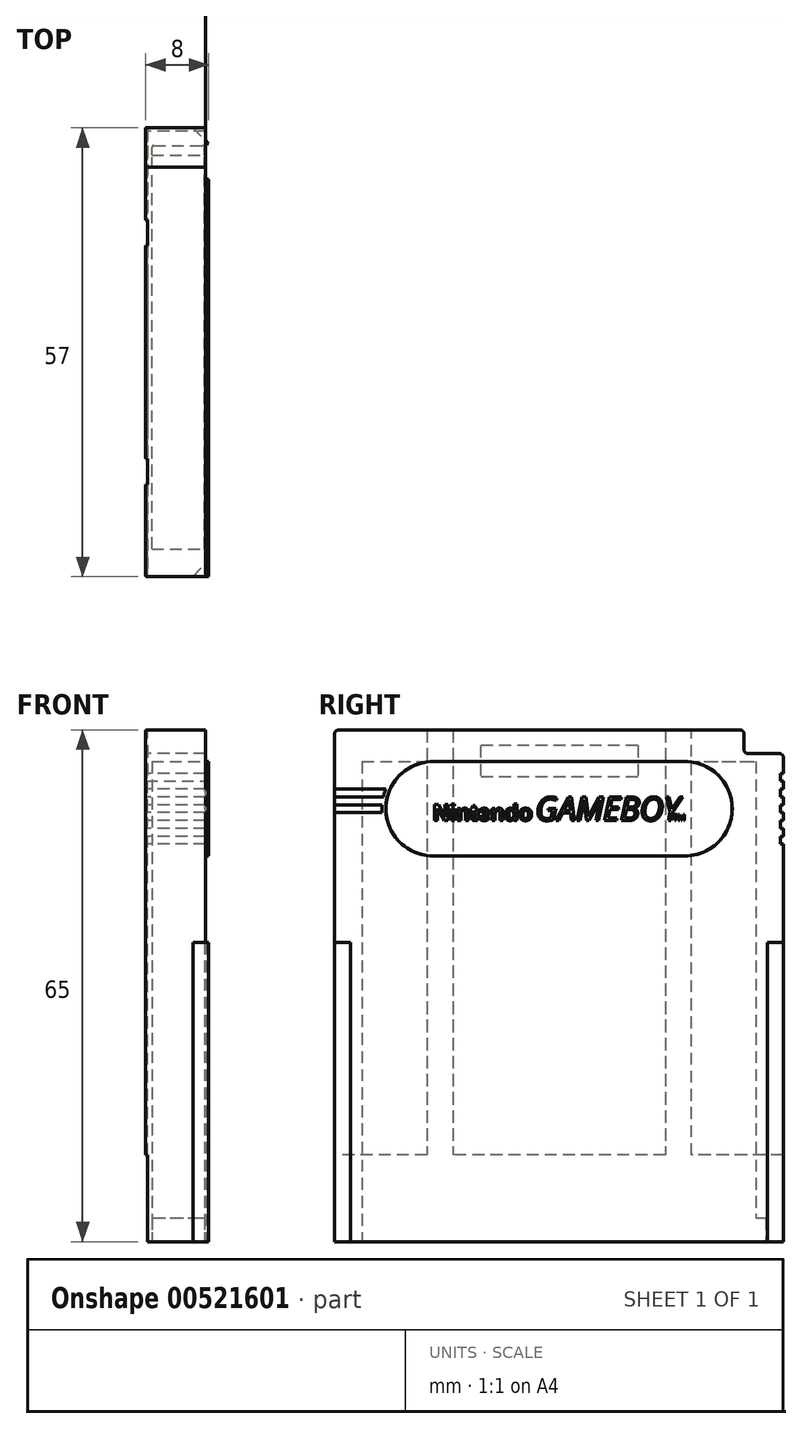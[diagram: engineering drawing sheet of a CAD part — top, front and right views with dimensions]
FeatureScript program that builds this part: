
annotation { "Feature Type Name" : "Feature", "Feature Type Description" : "" }
export const myFeature = defineFeature(function(context is Context, id is Id, definition is map)
    precondition{}
    {
        {
            var Q0;
            Q0=qCreatedBy(makeId("Right.planeOp"),FACE);
            var sketch = newSketch(context, id + "F0", { "sketchPlane" : qUnion([Q0])});
            skLineSegment(sketch, "E0.bottom", {"start": v(-28.5, 32.5) * mm, "end": v(23.5, 32.5) * mm});
            skLineSegment(sketch, "E0.top", {"start": v(-28.5, -32.5) * mm, "end": v(28.5, -32.5) * mm});
            skLineSegment(sketch, "E0.left", {"start": v(-28.5, 32.5) * mm, "end": v(-28.5, -32.5) * mm});
            skLineSegment(sketch, "E0.right", {"start": v(28.5, 29.5) * mm, "end": v(28.5, -32.5) * mm});
            skPoint(sketch, "E0.middle", {"position": v(0, 0) * mm});
            skLineSegment(sketch, "E1", {"start": v(23.5, 32.5) * mm, "end": v(23.5, 29.5) * mm});
            skLineSegment(sketch, "E2", {"start": v(23.5, 29.5) * mm, "end": v(28.5, 29.5) * mm});
            skSolve(sketch);
        }
        {
            var Q0;
            Q0=makeQuery(id+"F0.imprint","IMPRINT",FACE,{"disambiguationData":[TD([[makeQuery(id+"F0.imprint","IMPRINT",EDGE,{"derivedFrom":sQuery(id+"F0.wireOp",EDGE,"E0.bottom")}),-1.0]])]});
            extrude(context, id + "F1", {"entities" : qUnion([Q0]), "endBound" : BoundingType.SYMMETRIC, "depth" : 7.75 * mm, "offsetDistance" : 25 * mm});
        }
        {
            var Q0;
            Q0=makeQuery(id+"F1.opExtrude","SWEPT_FACE",FACE,{"disambiguationData":[OSD([sQuery(id+"F0.wireOp",EDGE,"E0.top")])]});
            var sketch = newSketch(context, id + "F2", { "sketchPlane" : qUnion([Q0])});
            skLineSegment(sketch, "E3", {"start": v(1.88, 28.5) * mm, "end": v(3.88, 26.5) * mm});
            skLineSegment(sketch, "E4", {"start": v(3.88, 26.5) * mm, "end": v(3.88, 28.5) * mm});
            skLineSegment(sketch, "E5", {"start": v(3.88, 28.5) * mm, "end": v(1.88, 28.5) * mm});
            skLineSegment(sketch, "E6", {"start": v(1.88, -28.5) * mm, "end": v(3.88, -26.5) * mm});
            skLineSegment(sketch, "E7", {"start": v(3.88, -26.5) * mm, "end": v(3.88, -28.5) * mm});
            skLineSegment(sketch, "E8", {"start": v(3.88, -28.5) * mm, "end": v(1.88, -28.5) * mm});
            skSolve(sketch);
        }
        {
            var Q0;
            Q0 = qSketchRegion(id + "F2", true);
            extrude(context, id + "F3", {"entities" : qUnion([Q0]), "operationType" : NewBodyOperationType.REMOVE, "oppositeDirection" : true, "depth" : 38 * mm, "offsetDistance" : 25 * mm});
        }
        {
            var Q0;
            Q0=makeQuery(id+"F1.opExtrude","CAP_FACE",FACE,{"disambiguationData":[OSD([sQuery(id+"F0.wireOp",EDGE,"E0.bottom"),sQuery(id+"F0.wireOp",EDGE,"E0.top"),sQuery(id+"F0.wireOp",EDGE,"E0.left"),sQuery(id+"F0.wireOp",EDGE,"E0.right"),sQuery(id+"F0.wireOp",EDGE,"E1"),sQuery(id+"F0.wireOp",EDGE,"E2")])],"isStart":true});
            var sketch = newSketch(context, id + "F4", { "sketchPlane" : qUnion([Q0])});
            skLineSegment(sketch, "E9.bottom", {"start": v(-13.5, 32.5) * mm, "end": v(13.5, 32.5) * mm});
            skLineSegment(sketch, "E9.top", {"start": v(-13.5, -21.5) * mm, "end": v(13.5, -21.5) * mm});
            skLineSegment(sketch, "E9.left", {"start": v(-13.5, 32.5) * mm, "end": v(-13.5, -21.5) * mm});
            skLineSegment(sketch, "E9.right", {"start": v(13.5, 32.5) * mm, "end": v(13.5, -21.5) * mm});
            skLineSegment(sketch, "E10.bottom", {"start": v(16.8, 32.5) * mm, "end": v(28.5, 32.5) * mm});
            skLineSegment(sketch, "E10.top", {"start": v(16.8, -21.5) * mm, "end": v(28.5, -21.5) * mm});
            skLineSegment(sketch, "E10.left", {"start": v(16.8, 32.5) * mm, "end": v(16.8, -21.5) * mm});
            skLineSegment(sketch, "E10.right", {"start": v(28.5, 32.5) * mm, "end": v(28.5, -21.5) * mm});
            skLineSegment(sketch, "E11.bottom", {"start": v(-28.5, -21.5) * mm, "end": v(-16.8, -21.5) * mm});
            skLineSegment(sketch, "E11.top", {"start": v(-23.5, 32.5) * mm, "end": v(-16.8, 32.5) * mm});
            skLineSegment(sketch, "E11.left", {"start": v(-28.5, -21.5) * mm, "end": v(-28.5, 29.5) * mm});
            skLineSegment(sketch, "E11.right", {"start": v(-16.8, -21.5) * mm, "end": v(-16.8, 32.5) * mm});
            skLineSegment(sketch, "E12", {"start": v(-28.5, 29.5) * mm, "end": v(-23.5, 29.5) * mm});
            skLineSegment(sketch, "E13", {"start": v(-23.5, 29.5) * mm, "end": v(-23.5, 32.5) * mm});
            skLineSegment(sketch, "E14.bottom", {"start": v(-10, 30.5) * mm, "end": v(10, 30.5) * mm});
            skLineSegment(sketch, "E14.top", {"start": v(-10, 26.5) * mm, "end": v(10, 26.5) * mm});
            skLineSegment(sketch, "E14.left", {"start": v(-10, 30.5) * mm, "end": v(-10, 26.5) * mm});
            skLineSegment(sketch, "E14.right", {"start": v(10, 30.5) * mm, "end": v(10, 26.5) * mm});
            skSolve(sketch);
        }
        {
            var Q0;
            Q0 = qSketchRegion(id + "F4", true);
            extrude(context, id + "F5", {"entities" : qUnion([Q0]), "operationType" : NewBodyOperationType.ADD, "depth" : .25 * mm, "offsetDistance" : 25 * mm});
        }
        {
            var Q0;
            Q0=makeQuery(id+"F1.opExtrude","CAP_FACE",FACE,{"disambiguationData":[OSD([sQuery(id+"F0.wireOp",EDGE,"E0.bottom"),sQuery(id+"F0.wireOp",EDGE,"E0.top"),sQuery(id+"F0.wireOp",EDGE,"E0.left"),sQuery(id+"F0.wireOp",EDGE,"E0.right"),sQuery(id+"F0.wireOp",EDGE,"E1"),sQuery(id+"F0.wireOp",EDGE,"E2")])],"isStart":false});
            var sketch = newSketch(context, id + "F6", { "sketchPlane" : qUnion([Q0])});
            skLineSegment(sketch, "E15.bottom", {"start": v(-16, 28.5) * mm, "end": v(16, 28.5) * mm});
            skLineSegment(sketch, "E15.top", {"start": v(-16, 16.5) * mm, "end": v(16, 16.5) * mm});
            skPoint(sketch, "E15.middle", {"position": v(0, 22.5) * mm});
            skArc(sketch, "E16", {"start": v(16, 16.5) * mm, "mid": v(22, 22.5) * mm, "end": v(16, 28.5) * mm});
            skArc(sketch, "E17", {"start": v(-16, 28.5) * mm, "mid": v(-22, 22.5) * mm, "end": v(-16, 16.5) * mm});
            skSolve(sketch);
        }
        {
            var Q0;
            Q0=makeQuery(id+"F6.imprint","IMPRINT",FACE,{"disambiguationData":[TD([[makeQuery(id+"F6.imprint","IMPRINT",EDGE,{"derivedFrom":sQuery(id+"F6.wireOp",EDGE,"E15.bottom")}),-1.0]])]});
            extrude(context, id + "F7", {"entities" : qUnion([Q0]), "operationType" : NewBodyOperationType.REMOVE, "oppositeDirection" : true, "depth" : .4 * mm, "offsetDistance" : 25 * mm});
        }
        {
            var Q0;
            Q0=makeQuery(id+"F7.boolean.opBoolean","COPY",FACE,{"derivedFrom":makeQuery(id+"F7.opExtrude","CAP_FACE",FACE,{"disambiguationData":[OSD([sQuery(id+"F6.wireOp",EDGE,"E15.bottom"),sQuery(id+"F6.wireOp",EDGE,"E15.top"),sQuery(id+"F6.wireOp",EDGE,"E16"),sQuery(id+"F6.wireOp",EDGE,"E17")])],"isStart":false})});
            fillet(context, id + "F8", {"entities" : qUnion([Q0]), "radius" : 10 * mm, "rho" : .5, "crossSection" : FilletCrossSection.CONIC, "allowEdgeOverflow" : false});
        }
        {
            var Q0;
            Q0=makeQuery(id+"F1.opExtrude","CAP_FACE",FACE,{"disambiguationData":[OSD([sQuery(id+"F0.wireOp",EDGE,"E0.bottom"),sQuery(id+"F0.wireOp",EDGE,"E0.top"),sQuery(id+"F0.wireOp",EDGE,"E0.left"),sQuery(id+"F0.wireOp",EDGE,"E0.right"),sQuery(id+"F0.wireOp",EDGE,"E1"),sQuery(id+"F0.wireOp",EDGE,"E2")])],"isStart":false});
            var sketch = newSketch(context, id + "F9", { "sketchPlane" : qUnion([Q0])});
            skArc(sketch, "E18", {"start": v(20.7, 18) * mm, "mid": v(21.1, 18.48) * mm, "end": v(21.48, 19) * mm});
            skLineSegment(sketch, "E19", {"start": v(20.7, 27) * mm, "end": v(28.5, 27) * mm});
            skLineSegment(sketch, "E20", {"start": v(28.5, 27) * mm, "end": v(28.5, 26) * mm});
            skLineSegment(sketch, "E21", {"start": v(28.5, 26) * mm, "end": v(21.48, 26) * mm});
            skLineSegment(sketch, "E22", {"start": v(22, 25) * mm, "end": v(28.5, 25) * mm});
            skLineSegment(sketch, "E23", {"start": v(28.5, 25) * mm, "end": v(28.5, 24) * mm});
            skLineSegment(sketch, "E24", {"start": v(28.5, 24) * mm, "end": v(22.32, 24) * mm});
            skLineSegment(sketch, "E25", {"start": v(22.48, 23) * mm, "end": v(28.5, 23) * mm});
            skLineSegment(sketch, "E26", {"start": v(28.5, 23) * mm, "end": v(28.5, 22) * mm});
            skLineSegment(sketch, "E27", {"start": v(28.5, 22) * mm, "end": v(22.48, 22) * mm});
            skLineSegment(sketch, "E28", {"start": v(22.32, 21) * mm, "end": v(28.5, 21) * mm});
            skLineSegment(sketch, "E29", {"start": v(21.48, 19) * mm, "end": v(28.5, 19) * mm});
            skLineSegment(sketch, "E30", {"start": v(28.5, 21) * mm, "end": v(28.5, 20) * mm});
            skLineSegment(sketch, "E31", {"start": v(28.5, 20) * mm, "end": v(22, 20) * mm});
            skLineSegment(sketch, "E32", {"start": v(28.5, 19) * mm, "end": v(28.5, 18) * mm});
            skLineSegment(sketch, "E33", {"start": v(28.5, 18) * mm, "end": v(20.7, 18) * mm});
            skArc(sketch, "E34.trimOffspring", {"start": v(21.48, 26) * mm, "mid": v(21.1, 26.52) * mm, "end": v(20.7, 27) * mm});
            skArc(sketch, "E35.trimOffspring", {"start": v(22.32, 24) * mm, "mid": v(22.18, 24.5) * mm, "end": v(22, 25) * mm});
            skArc(sketch, "E36.trimOffspring", {"start": v(22.48, 22) * mm, "mid": v(22.5, 22.5) * mm, "end": v(22.48, 23) * mm});
            skArc(sketch, "E37.trimOffspring", {"start": v(22, 20) * mm, "mid": v(22.18, 20.5) * mm, "end": v(22.32, 21) * mm});
            skArc(sketch, "E38.MirrorCS", {"start": v(-22.48, 22) * mm, "mid": v(-22.5, 22.5) * mm, "end": v(-22.48, 23) * mm});
            skLineSegment(sketch, "E39.MirrorCS", {"start": v(-28.5, 23) * mm, "end": v(-28.5, 22) * mm});
            skLineSegment(sketch, "E40.MirrorCS", {"start": v(-28.5, 21) * mm, "end": v(-28.5, 20) * mm});
            skArc(sketch, "E41.MirrorCS", {"start": v(-22, 20) * mm, "mid": v(-22.18, 20.5) * mm, "end": v(-22.32, 21) * mm});
            skArc(sketch, "E42.MirrorCS", {"start": v(-22.32, 24) * mm, "mid": v(-22.18, 24.5) * mm, "end": v(-22, 25) * mm});
            skLineSegment(sketch, "E43.MirrorCS", {"start": v(-28.5, 19) * mm, "end": v(-28.5, 18) * mm});
            skLineSegment(sketch, "E44.MirrorCS", {"start": v(-28.5, 25) * mm, "end": v(-28.5, 24) * mm});
            skLineSegment(sketch, "E45.MirrorCS", {"start": v(-28.5, 27) * mm, "end": v(-28.5, 26) * mm});
            skArc(sketch, "E46.MirrorCS", {"start": v(-21.48, 26) * mm, "mid": v(-21.1, 26.52) * mm, "end": v(-20.7, 27) * mm});
            skArc(sketch, "E47.MirrorCS", {"start": v(-20.7, 18) * mm, "mid": v(-21.1, 18.48) * mm, "end": v(-21.48, 19) * mm});
            skLineSegment(sketch, "E48.MirrorCS", {"start": v(-28.5, 18) * mm, "end": v(-20.7, 18) * mm});
            skLineSegment(sketch, "E49.MirrorCS", {"start": v(-20.7, 27) * mm, "end": v(-28.5, 27) * mm});
            skLineSegment(sketch, "E50.MirrorCS", {"start": v(-28.5, 26) * mm, "end": v(-21.48, 26) * mm});
            skLineSegment(sketch, "E51.MirrorCS", {"start": v(-22, 25) * mm, "end": v(-28.5, 25) * mm});
            skLineSegment(sketch, "E52.MirrorCS", {"start": v(-28.5, 24) * mm, "end": v(-22.32, 24) * mm});
            skLineSegment(sketch, "E53.MirrorCS", {"start": v(-22.48, 23) * mm, "end": v(-28.5, 23) * mm});
            skLineSegment(sketch, "E54.MirrorCS", {"start": v(-21.48, 19) * mm, "end": v(-28.5, 19) * mm});
            skLineSegment(sketch, "E55.MirrorCS", {"start": v(-28.5, 20) * mm, "end": v(-22, 20) * mm});
            skLineSegment(sketch, "E56.MirrorCS", {"start": v(-22.32, 21) * mm, "end": v(-28.5, 21) * mm});
            skLineSegment(sketch, "E57.MirrorCS", {"start": v(-28.5, 22) * mm, "end": v(-22.48, 22) * mm});
            skSolve(sketch);
        }
        {
            var Q0;
            Q0=makeQuery(id+"F9.imprint","IMPRINT",FACE,{"disambiguationData":[TD([[makeQuery(id+"F9.imprint","IMPRINT",EDGE,{"derivedFrom":sQuery(id+"F9.wireOp",EDGE,"E43.MirrorCS")}),1.0]])]});
            var Q1;
            Q1=makeQuery(id+"F9.imprint","IMPRINT",FACE,{"disambiguationData":[TD([[makeQuery(id+"F9.imprint","IMPRINT",EDGE,{"derivedFrom":sQuery(id+"F9.wireOp",EDGE,"E40.MirrorCS")}),1.0]])]});
            var Q2;
            Q2=makeQuery(id+"F9.imprint","IMPRINT",FACE,{"disambiguationData":[TD([[makeQuery(id+"F9.imprint","IMPRINT",EDGE,{"derivedFrom":sQuery(id+"F9.wireOp",EDGE,"E38.MirrorCS")}),1.0]])]});
            var Q3;
            Q3=makeQuery(id+"F9.imprint","IMPRINT",FACE,{"disambiguationData":[TD([[makeQuery(id+"F9.imprint","IMPRINT",EDGE,{"derivedFrom":sQuery(id+"F9.wireOp",EDGE,"E42.MirrorCS")}),1.0]])]});
            var Q4;
            Q4=makeQuery(id+"F9.imprint","IMPRINT",FACE,{"disambiguationData":[TD([[makeQuery(id+"F9.imprint","IMPRINT",EDGE,{"derivedFrom":sQuery(id+"F9.wireOp",EDGE,"E45.MirrorCS")}),1.0]])]});
            var Q5;
            Q5=makeQuery(id+"F9.imprint","IMPRINT",FACE,{"disambiguationData":[TD([[makeQuery(id+"F9.imprint","IMPRINT",EDGE,{"derivedFrom":sQuery(id+"F9.wireOp",EDGE,"E19")}),-1.0]])]});
            var Q6;
            Q6=makeQuery(id+"F9.imprint","IMPRINT",FACE,{"disambiguationData":[TD([[makeQuery(id+"F9.imprint","IMPRINT",EDGE,{"derivedFrom":sQuery(id+"F9.wireOp",EDGE,"E22")}),-1.0]])]});
            var Q7;
            Q7=makeQuery(id+"F9.imprint","IMPRINT",FACE,{"disambiguationData":[TD([[makeQuery(id+"F9.imprint","IMPRINT",EDGE,{"derivedFrom":sQuery(id+"F9.wireOp",EDGE,"E25")}),-1.0]])]});
            var Q8;
            Q8=makeQuery(id+"F9.imprint","IMPRINT",FACE,{"disambiguationData":[TD([[makeQuery(id+"F9.imprint","IMPRINT",EDGE,{"derivedFrom":sQuery(id+"F9.wireOp",EDGE,"E28")}),-1.0]])]});
            var Q9;
            Q9=makeQuery(id+"F9.imprint","IMPRINT",FACE,{"disambiguationData":[TD([[makeQuery(id+"F9.imprint","IMPRINT",EDGE,{"derivedFrom":sQuery(id+"F9.wireOp",EDGE,"E18")}),-1.0]])]});
            extrude(context, id + "F10", {"entities" : qUnion([Q0, Q1, Q2, Q3, Q4, Q5, Q6, Q7, Q8, Q9]), "operationType" : NewBodyOperationType.REMOVE, "oppositeDirection" : true, "depth" : .4 * mm, "offsetDistance" : 25 * mm});
        }
        {
            var Q0;
            Q0=makeQuery(id+"F5.boolean.opBoolean","MERGE",FACE,{"derivedFrom":[makeQuery(id+"F1.opExtrude","SWEPT_FACE",FACE,{"disambiguationData":[OSD([sQuery(id+"F0.wireOp",EDGE,"E0.right")])]}),makeQuery(id+"F5.opExtrude","SWEPT_FACE",FACE,{"disambiguationData":[OSD([sQuery(id+"F4.wireOp",EDGE,"E11.left")])]})]});
            var sketch = newSketch(context, id + "F11", { "sketchPlane" : qUnion([Q0])});
            skLineSegment(sketch, "E58", {"start": v(-3.48, 27) * mm, "end": v(4.12, 27) * mm});
            skLineSegment(sketch, "E59", {"start": v(4.12, 27) * mm, "end": v(4.12, 26) * mm});
            skLineSegment(sketch, "E60", {"start": v(4.12, 26) * mm, "end": v(-3.47, 26) * mm});
            skLineSegment(sketch, "E61", {"start": v(-3.47, 26) * mm, "end": v(-3.47, 27) * mm});
            skLineSegment(sketch, "E62.bottom", {"start": v(-3.48, 25) * mm, "end": v(4.12, 25) * mm});
            skLineSegment(sketch, "E62.top", {"start": v(-3.48, 24) * mm, "end": v(4.12, 24) * mm});
            skLineSegment(sketch, "E62.left", {"start": v(-3.47, 25) * mm, "end": v(-3.47, 24) * mm});
            skLineSegment(sketch, "E62.right", {"start": v(4.12, 25) * mm, "end": v(4.12, 24) * mm});
            skLineSegment(sketch, "E63.bottom", {"start": v(-3.48, 23) * mm, "end": v(4.12, 23) * mm});
            skLineSegment(sketch, "E63.top", {"start": v(-3.48, 22) * mm, "end": v(4.12, 22) * mm});
            skLineSegment(sketch, "E63.left", {"start": v(-3.48, 23) * mm, "end": v(-3.48, 22) * mm});
            skLineSegment(sketch, "E63.right", {"start": v(4.12, 23) * mm, "end": v(4.12, 22) * mm});
            skLineSegment(sketch, "E64.bottom", {"start": v(-3.48, 21) * mm, "end": v(4.12, 21) * mm});
            skLineSegment(sketch, "E64.top", {"start": v(-3.48, 20) * mm, "end": v(4.12, 20) * mm});
            skLineSegment(sketch, "E64.left", {"start": v(-3.47, 21) * mm, "end": v(-3.47, 20) * mm});
            skLineSegment(sketch, "E64.right", {"start": v(4.12, 21) * mm, "end": v(4.12, 20) * mm});
            skLineSegment(sketch, "E65.bottom", {"start": v(-3.48, 19) * mm, "end": v(4.12, 19) * mm});
            skLineSegment(sketch, "E65.top", {"start": v(-3.48, 18) * mm, "end": v(4.12, 18) * mm});
            skLineSegment(sketch, "E65.left", {"start": v(-3.47, 19) * mm, "end": v(-3.47, 18) * mm});
            skLineSegment(sketch, "E65.right", {"start": v(4.12, 19) * mm, "end": v(4.12, 18) * mm});
            skSolve(sketch);
        }
        {
            var Q0;
            Q0 = qSketchRegion(id + "F11", true);
            extrude(context, id + "F12", {"entities" : qUnion([Q0]), "operationType" : NewBodyOperationType.REMOVE, "oppositeDirection" : true, "depth" : .4 * mm, "offsetDistance" : 25 * mm});
        }
        {
            var Q0;
            Q0=makeQuery(id+"F5.boolean.opBoolean","MERGE",EDGE,{"derivedFrom":[makeQuery(id+"F1.opExtrude","SWEPT_EDGE",EDGE,{"disambiguationData":[OSD([sQuery(id+"F0.wireOp",EDGE,"E0.bottom"),sQuery(id+"F0.wireOp",EDGE,"E1")])]}),makeQuery(id+"F5.opExtrude","SWEPT_EDGE",EDGE,{"disambiguationData":[OSD([sQuery(id+"F4.wireOp",EDGE,"E11.top"),sQuery(id+"F4.wireOp",EDGE,"E13")])]})]});
            var Q1;
            Q1=makeQuery(id+"F5.boolean.opBoolean","MERGE",EDGE,{"derivedFrom":[makeQuery(id+"F1.opExtrude","SWEPT_EDGE",EDGE,{"disambiguationData":[OSD([sQuery(id+"F0.wireOp",EDGE,"E1"),sQuery(id+"F0.wireOp",EDGE,"E2")])]}),makeQuery(id+"F5.opExtrude","SWEPT_EDGE",EDGE,{"disambiguationData":[OSD([sQuery(id+"F4.wireOp",EDGE,"E12"),sQuery(id+"F4.wireOp",EDGE,"E13")])]})]});
            var Q2;
            Q2=makeQuery(id+"F5.boolean.opBoolean","MERGE",EDGE,{"derivedFrom":[makeQuery(id+"F1.opExtrude","SWEPT_EDGE",EDGE,{"disambiguationData":[OSD([sQuery(id+"F0.wireOp",EDGE,"E0.right"),sQuery(id+"F0.wireOp",EDGE,"E2")])]}),makeQuery(id+"F5.opExtrude","SWEPT_EDGE",EDGE,{"disambiguationData":[OSD([sQuery(id+"F4.wireOp",EDGE,"E11.left"),sQuery(id+"F4.wireOp",EDGE,"E12")])]})]});
            var Q3;
            Q3=makeQuery(id+"F5.boolean.opBoolean","MERGE",EDGE,{"derivedFrom":[makeQuery(id+"F1.opExtrude","SWEPT_EDGE",EDGE,{"disambiguationData":[OSD([sQuery(id+"F0.wireOp",EDGE,"E0.bottom"),sQuery(id+"F0.wireOp",EDGE,"E0.left")])]}),makeQuery(id+"F5.opExtrude","SWEPT_EDGE",EDGE,{"disambiguationData":[OSD([sQuery(id+"F4.wireOp",EDGE,"E10.bottom"),sQuery(id+"F4.wireOp",EDGE,"E10.right")])]})]});
            fillet(context, id + "F13", {"entities" : qUnion([Q0, Q1, Q2, Q3]), "radius" : .5 * mm, "tangentPropagation" : true, "allowEdgeOverflow" : false});
        }
        {
            var Q0;
            Q0=makeQuery(id+"F1.opExtrude","CAP_EDGE",EDGE,{"disambiguationData":[OSD([sQuery(id+"F0.wireOp",EDGE,"E0.bottom")])],"isStart":false});
            var Q1;
            Q1=makeQuery(id+"F1.opExtrude","CAP_EDGE",EDGE,{"disambiguationData":[OSD([sQuery(id+"F0.wireOp",EDGE,"E2")])],"isStart":false});
            var Q2;
            Q2=makeQuery(id+"F5.opExtrude","CAP_EDGE",EDGE,{"disambiguationData":[OSD([sQuery(id+"F4.wireOp",EDGE,"E12")])],"isStart":false});
            var Q3;
            Q3=makeQuery(id+"F5.opExtrude","CAP_EDGE",EDGE,{"disambiguationData":[OSD([sQuery(id+"F4.wireOp",EDGE,"E13")])],"isStart":false});
            var Q4;
            Q4=makeQuery(id+"F1.opExtrude","CAP_EDGE",EDGE,{"disambiguationData":[OSD([sQuery(id+"F0.wireOp",EDGE,"E1")])],"isStart":false});
            var Q5;
            Q5=makeQuery(id+"F5.opExtrude","CAP_EDGE",EDGE,{"disambiguationData":[OSD([sQuery(id+"F4.wireOp",EDGE,"E11.top")])],"isStart":false});
            var Q6;
            Q6=makeQuery(id+"F5.opExtrude","CAP_EDGE",EDGE,{"disambiguationData":[OSD([sQuery(id+"F4.wireOp",EDGE,"E9.bottom")])],"isStart":false});
            var Q7;
            Q7=makeQuery(id+"F5.opExtrude","CAP_EDGE",EDGE,{"disambiguationData":[OSD([sQuery(id+"F4.wireOp",EDGE,"E10.bottom")])],"isStart":false});
            var Q8;
            {var subQ0=sQuery(id+"F4.wireOp",EDGE,"E10.right");Q8=makeQuery(id+"FrGKLvruxDWx0Zx_1.1.F12.boolean.opBoolean","SPLIT",EDGE,{"disambiguationData":[TD([makeQuery(id+"F1.opExtrude","SWEPT_FACE",FACE,{"disambiguationData":[OSD([sQuery(id+"F0.wireOp",EDGE,"E0.bottom")])]})])],"derivedFrom":makeQuery(id+"F5.opExtrude","CAP_EDGE",EDGE,{"disambiguationData":[OSD([subQ0])],"isStart":false})});}
            var Q9;
            {var subQ0=sQuery(id+"F0.wireOp",EDGE,"E0.left");var subQ1=sQuery(id+"F0.wireOp",EDGE,"E0.bottom");Q9=makeQuery(id+"F10.boolean.opBoolean","SPLIT",EDGE,{"disambiguationData":[TD([makeQuery(id+"F1.opExtrude","SWEPT_FACE",FACE,{"disambiguationData":[OSD([subQ1])]})])],"derivedFrom":makeQuery(id+"F1.opExtrude","CAP_EDGE",EDGE,{"disambiguationData":[OSD([subQ0])],"isStart":false})});}
            var Q10;
            {var subQ0=sQuery(id+"F0.wireOp",EDGE,"E0.left");Q10=makeQuery(id+"F10.boolean.opBoolean","SPLIT",EDGE,{"disambiguationData":[TD([makeQuery(id+"F10.opExtrude","SWEPT_FACE",FACE,{"disambiguationData":[OSD([sQuery(id+"F9.wireOp",EDGE,"E48.MirrorCS")])]})])],"derivedFrom":makeQuery(id+"F1.opExtrude","CAP_EDGE",EDGE,{"disambiguationData":[OSD([subQ0])],"isStart":false})});}
            var Q11;
            {var subQ0=sQuery(id+"F4.wireOp",EDGE,"E10.top");var subQ1=sQuery(id+"F4.wireOp",EDGE,"E10.right");Q11=makeQuery(id+"FrGKLvruxDWx0Zx_1.1.F12.boolean.opBoolean","SPLIT",EDGE,{"disambiguationData":[TD([makeQuery(id+"F5.opExtrude","SWEPT_FACE",FACE,{"disambiguationData":[OSD([subQ0])]})])],"derivedFrom":makeQuery(id+"F5.opExtrude","CAP_EDGE",EDGE,{"disambiguationData":[OSD([subQ1])],"isStart":false})});}
            var Q12;
            {var subQ0=sQuery(id+"F0.wireOp",EDGE,"E0.right");Q12=makeQuery(id+"F10.boolean.opBoolean","SPLIT",EDGE,{"disambiguationData":[TD([makeQuery(id+"F10.opExtrude","SWEPT_FACE",FACE,{"disambiguationData":[OSD([sQuery(id+"F9.wireOp",EDGE,"E33")])]})])],"derivedFrom":makeQuery(id+"F1.opExtrude","CAP_EDGE",EDGE,{"disambiguationData":[OSD([subQ0])],"isStart":false})});}
            var Q13;
            {var subQ0=sQuery(id+"F4.wireOp",EDGE,"E11.left");var subQ1=sQuery(id+"F4.wireOp",EDGE,"E11.bottom");Q13=makeQuery(id+"F12.boolean.opBoolean","SPLIT",EDGE,{"disambiguationData":[TD([makeQuery(id+"F5.opExtrude","SWEPT_FACE",FACE,{"disambiguationData":[OSD([subQ1])]})])],"derivedFrom":makeQuery(id+"F5.opExtrude","CAP_EDGE",EDGE,{"disambiguationData":[OSD([subQ0])],"isStart":false})});}
            fillet(context, id + "F14", {"entities" : qUnion([Q0, Q1, Q2, Q3, Q4, Q5, Q6, Q7, Q8, Q9, Q10, Q11, Q12, Q13]), "radius" : .1 * mm, "tangentPropagation" : true, "allowEdgeOverflow" : false});
        }
        {
            var Q0;
            Q0=makeQuery(id+"F7.boolean.opBoolean","COPY",FACE,{"derivedFrom":makeQuery(id+"F7.opExtrude","CAP_FACE",FACE,{"disambiguationData":[OSD([sQuery(id+"F6.wireOp",EDGE,"E15.bottom"),sQuery(id+"F6.wireOp",EDGE,"E15.top"),sQuery(id+"F6.wireOp",EDGE,"E16"),sQuery(id+"F6.wireOp",EDGE,"E17")])],"isStart":false})});
            var sketch = newSketch(context, id + "F15", { "sketchPlane" : qUnion([Q0])});
            skText(sketch, "E66", { "text": "Nintendo", "fontName": "Arimo-Bold.ttf"});
            skText(sketch, "E67", { "text": "GAMEBOY", "fontName": "OpenSans-Italic.ttf"});
            skText(sketch, "E68", { "text": "TM", "fontName": "OpenSans-Regular.ttf"});
            const initialGuessF15  = {"E66": [-0.016, 0.021, 1, 0, 0.0021], "E67": [-0.003, 0.021, 1, 0, 0.003], "E68": [0.0145, 0.021, 1, 0, 0.00076]};
            skSetInitialGuess(sketch, initialGuessF15);
            skSolve(sketch);
        }
        {
            var Q0;
            Q0 = qSketchRegion(id + "F15", true);
            extrude(context, id + "F16", {"entities" : qUnion([Q0]), "operationType" : NewBodyOperationType.ADD, "depth" : .1 * mm, "offsetDistance" : 25 * mm});
        }
        {
            var Q0;
            Q0=makeQuery(id+"F1.opExtrude","CAP_FACE",FACE,{"disambiguationData":[OSD([sQuery(id+"F0.wireOp",EDGE,"E0.bottom"),sQuery(id+"F0.wireOp",EDGE,"E0.top"),sQuery(id+"F0.wireOp",EDGE,"E0.left"),sQuery(id+"F0.wireOp",EDGE,"E0.right"),sQuery(id+"F0.wireOp",EDGE,"E1"),sQuery(id+"F0.wireOp",EDGE,"E2")])],"isStart":false});
            var sketch = newSketch(context, id + "F17", { "sketchPlane" : qUnion([Q0])});
            skLineSegment(sketch, "E69.bottom", {"start": v(-21.75, 14.75) * mm, "end": v(21.75, 14.75) * mm});
            skLineSegment(sketch, "E69.top", {"start": v(-21.75, -24.75) * mm, "end": v(21.75, -24.75) * mm});
            skLineSegment(sketch, "E69.left", {"start": v(-22, 14.5) * mm, "end": v(-22, -24.5) * mm});
            skLineSegment(sketch, "E69.right", {"start": v(22, 14.5) * mm, "end": v(22, -24.5) * mm});
            skPoint(sketch, "E69.middle", {"position": v(0, -5) * mm});
            skLineSegment(sketch, "E70", {"start": v(-3.94, -26.05) * mm, "end": v(3.94, -26.05) * mm});
            skLineSegment(sketch, "E71", {"start": v(4.12, -26.47) * mm, "end": v(0.19, -30.84) * mm});
            skLineSegment(sketch, "E72", {"start": v(-0.19, -30.84) * mm, "end": v(-4.12, -26.47) * mm});
            skPoint(sketch, "E73.visualSharp", {"position": v(-22, 14.75) * mm});
            skArc(sketch, "E73.filletArc", {"start": v(-21.75, 14.75) * mm, "mid": v(-21.93, 14.68) * mm, "end": v(-22, 14.5) * mm});
            skPoint(sketch, "E74.visualSharp", {"position": v(22, 14.75) * mm});
            skArc(sketch, "E74.filletArc", {"start": v(22, 14.5) * mm, "mid": v(21.93, 14.68) * mm, "end": v(21.75, 14.75) * mm});
            skPoint(sketch, "E75.visualSharp", {"position": v(-22, -24.75) * mm});
            skArc(sketch, "E75.filletArc", {"start": v(-22, -24.5) * mm, "mid": v(-21.93, -24.68) * mm, "end": v(-21.75, -24.75) * mm});
            skPoint(sketch, "E76.visualSharp", {"position": v(22, -24.75) * mm});
            skArc(sketch, "E76.filletArc", {"start": v(21.75, -24.75) * mm, "mid": v(21.93, -24.68) * mm, "end": v(22, -24.5) * mm});
            skPoint(sketch, "E77.visualSharp", {"position": v(-4.5, -26.05) * mm});
            skArc(sketch, "E77.filletArc", {"start": v(-3.94, -26.05) * mm, "mid": v(-4.17, -26.2) * mm, "end": v(-4.12, -26.47) * mm});
            skPoint(sketch, "E78.visualSharp", {"position": v(4.5, -26.05) * mm});
            skArc(sketch, "E78.filletArc", {"start": v(4.12, -26.47) * mm, "mid": v(4.17, -26.2) * mm, "end": v(3.94, -26.05) * mm});
            skPoint(sketch, "E79.visualSharp", {"position": v(0, -31.05) * mm});
            skArc(sketch, "E79.filletArc", {"start": v(-0.19, -30.84) * mm, "mid": v(0, -30.93) * mm, "end": v(0.19, -30.84) * mm});
            skSolve(sketch);
        }
        {
            var Q0;
            Q0 = qSketchRegion(id + "F17", true);
            extrude(context, id + "F18", {"entities" : qUnion([Q0]), "operationType" : NewBodyOperationType.REMOVE, "oppositeDirection" : true, "depth" : .1 * mm, "offsetDistance" : 25 * mm});
        }
        {
            var Q0;
            Q0=makeQuery(id+"F1.opExtrude","SWEPT_FACE",FACE,{"disambiguationData":[OSD([sQuery(id+"F0.wireOp",EDGE,"E0.top")])]});
            var sketch = newSketch(context, id + "F19", { "sketchPlane" : qUnion([Q0])});
            skLineSegment(sketch, "E80.bottom", {"start": v(-3.35, 25) * mm, "end": v(3.35, 25) * mm});
            skLineSegment(sketch, "E80.top", {"start": v(-3.35, -25) * mm, "end": v(3.35, -25) * mm});
            skLineSegment(sketch, "E80.left", {"start": v(-3.35, 25) * mm, "end": v(-3.35, -25) * mm});
            skLineSegment(sketch, "E80.right", {"start": v(3.35, 25) * mm, "end": v(3.35, -25) * mm});
            skPoint(sketch, "E80.middle", {"position": v(0, 0) * mm});
            skSolve(sketch);
        }
        {
            var Q0;
            Q0=makeQuery(id+"F19.imprint","IMPRINT",FACE,{"disambiguationData":[TD([[makeQuery(id+"F19.imprint","IMPRINT",EDGE,{"derivedFrom":sQuery(id+"F19.wireOp",EDGE,"E80.bottom")}),-1.0]])]});
            extrude(context, id + "F20", {"entities" : qUnion([Q0]), "operationType" : NewBodyOperationType.REMOVE, "oppositeDirection" : true, "depth" : 61 * mm, "offsetDistance" : 25 * mm});
        }
        {
            var Q0;
            Q0=makeQuery(id+"F1.opExtrude","SWEPT_FACE",FACE,{"disambiguationData":[OSD([sQuery(id+"F0.wireOp",EDGE,"E0.top")])]});
            var sketch = newSketch(context, id + "F21", { "sketchPlane" : qUnion([Q0])});
            skLineSegment(sketch, "E81.bottom", {"start": v(-3.35, -25) * mm, "end": v(3.35, -25) * mm});
            skLineSegment(sketch, "E81.top", {"start": v(-3.1, -26.25) * mm, "end": v(3.1, -26.25) * mm});
            skLineSegment(sketch, "E81.left", {"start": v(-3.35, -25) * mm, "end": v(-3.35, -26) * mm});
            skLineSegment(sketch, "E81.right", {"start": v(3.35, -25) * mm, "end": v(3.35, -26) * mm});
            skPoint(sketch, "E82.visualSharp", {"position": v(-3.35, -26.25) * mm});
            skArc(sketch, "E82.filletArc", {"start": v(-3.35, -26) * mm, "mid": v(-3.28, -26.18) * mm, "end": v(-3.1, -26.25) * mm});
            skPoint(sketch, "E83.visualSharp", {"position": v(3.35, -26.25) * mm});
            skArc(sketch, "E83.filletArc", {"start": v(3.1, -26.25) * mm, "mid": v(3.28, -26.18) * mm, "end": v(3.35, -26) * mm});
            skSolve(sketch);
        }
        {
            var Q0;
            Q0 = qSketchRegion(id + "F21", true);
            extrude(context, id + "F22", {"entities" : qUnion([Q0]), "operationType" : NewBodyOperationType.REMOVE, "oppositeDirection" : true, "depth" : 3 * mm, "offsetDistance" : 25 * mm});
        }
    });
